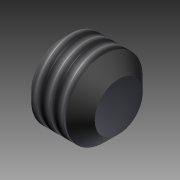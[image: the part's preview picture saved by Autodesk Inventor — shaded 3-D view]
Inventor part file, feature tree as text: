
AUTODESK INVENTOR PART (.ipt)
format: ipt  version: 2016 (Build 200138000, 138)  size: 125,440 bytes
history: native  units: mm
features: other x7, sketch x3, revolve x2, thread x1, extrude x1
ambient origin geometry x8: Origin, YZ Plane, XZ Plane, XY Plane, X Axis, Y Axis, Z Axis, Center Point
bodies: Solid1 (feature_tree)
feature tree (14):
  revolve  "Revolution1"  [1 undecoded]
  thread  "Thread1"  [1 undecoded]
  extrude  "Extrusion1"  TaperAngle=0.0deg  [1 undecoded]
  revolve  "Revolution2"  [1 undecoded]
  other  "CP_XY"
  other  "CP_YZ"
  other  "CP_ZX"
  other  "CP_X"
  other  "CP_Y"
  other  "CP_Z"
  other  "CP_Center"
  sketch  "Sketch_1"  dims[d0=360.0deg d1=1.8205mm d2=0.0mm d3=1.5mm d4=0.0mm]
  sketch  "Sketch_2"  dims[d5=360.0deg d6=0.0mm]
  sketch  "Sketch_3"
note: 4 required parameter values undecoded (feature->parameter linkage not recoverable at this tier; creation-order binding heuristic only, values carry confidence <= 0.55)